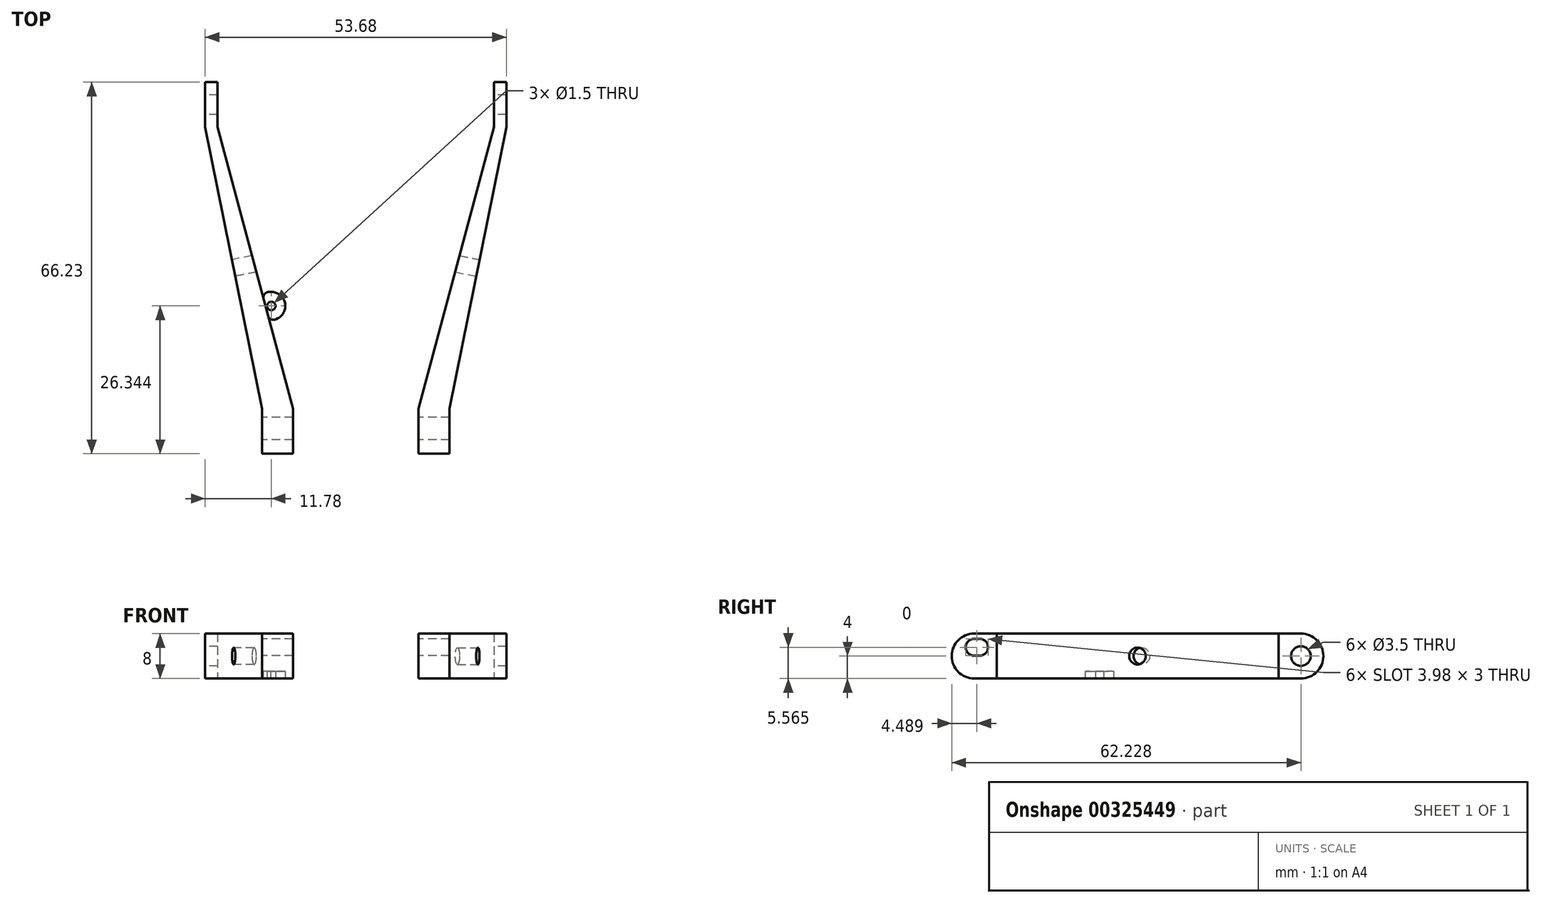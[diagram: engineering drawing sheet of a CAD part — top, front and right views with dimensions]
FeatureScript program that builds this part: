
annotation { "Feature Type Name" : "Feature", "Feature Type Description" : "" }
export const myFeature = defineFeature(function(context is Context, id is Id, definition is map)
    precondition{}
    {
        {
            var Q0;
            Q0=qCreatedBy(makeId("Top.planeOp"),FACE);
            var sketch = newSketch(context, id + "F0", { "sketchPlane" : qUnion([Q0])});
            skLineSegment(sketch, "E0.bottom", {"start": v(2.75, 4) * mm, "end": v(-2.75, 4) * mm});
            skLineSegment(sketch, "E0.top", {"start": v(2.75, -4) * mm, "end": v(-2.75, -4) * mm});
            skLineSegment(sketch, "E0.left", {"start": v(2.75, 4) * mm, "end": v(2.75, -4) * mm});
            skLineSegment(sketch, "E0.right", {"start": v(-2.75, 4) * mm, "end": v(-2.75, -4) * mm});
            skPoint(sketch, "E0.middle", {"position": v(0, 0) * mm});
            skLineSegment(sketch, "E1", {"start": v(2.75, 4) * mm, "end": v(-10.7, 54.23) * mm});
            skLineSegment(sketch, "E2.bottom", {"start": v(-10.7, 54.23) * mm, "end": v(-12.9, 54.23) * mm});
            skLineSegment(sketch, "E2.top", {"start": v(-10.7, 62.23) * mm, "end": v(-12.9, 62.23) * mm});
            skLineSegment(sketch, "E2.left", {"start": v(-10.7, 54.23) * mm, "end": v(-10.7, 62.23) * mm});
            skLineSegment(sketch, "E2.right", {"start": v(-12.9, 54.23) * mm, "end": v(-12.9, 62.23) * mm});
            skLineSegment(sketch, "E3", {"start": v(-12.9, 54.23) * mm, "end": v(-2.75, 4) * mm});
            skCircle(sketch, "E4", {"center": v(-1.13, 22.34) * mm, "radius": 0.75 * mm});
            skArc(sketch, "E5", {"start": v(0, 20.11) * mm, "mid": v(1.28, 23) * mm, "end": v(-1.28, 24.84) * mm});
            skLineSegment(sketch, "E6", {"start": v(-1.28, 24.84) * mm, "end": v(-2.83, 24.84) * mm});
            skLineSegment(sketch, "E7", {"start": v(-2.83, 24.84) * mm, "end": v(-1.38, 19.41) * mm});
            skLineSegment(sketch, "E8", {"start": v(-1.38, 19.41) * mm, "end": v(0, 20.11) * mm});
            skLineSegment(sketch, "E9", {"start": v(13.93, -16.72) * mm, "end": v(13.93, 66.12) * mm});
            skLineSegment(sketch, "E10.MirrorCS", {"start": v(38.57, 54.23) * mm, "end": v(38.57, 62.23) * mm});
            skLineSegment(sketch, "E11.MirrorCS", {"start": v(40.77, 54.23) * mm, "end": v(40.77, 62.23) * mm});
            skLineSegment(sketch, "E12.MirrorCS", {"start": v(40.77, 54.23) * mm, "end": v(30.6, 4) * mm});
            skLineSegment(sketch, "E13.MirrorCS", {"start": v(25.1, 4) * mm, "end": v(38.57, 54.23) * mm});
            skLineSegment(sketch, "E14.MirrorCS", {"start": v(25.1, 4) * mm, "end": v(25.1, -4) * mm});
            skLineSegment(sketch, "E15.MirrorCS", {"start": v(25.1, -4) * mm, "end": v(30.6, -4) * mm});
            skLineSegment(sketch, "E16.MirrorCS", {"start": v(30.6, 4) * mm, "end": v(30.6, -4) * mm});
            skArc(sketch, "E17.MirrorCS", {"start": v(27.86, 20.11) * mm, "mid": v(26.58, 23) * mm, "end": v(29.14, 24.84) * mm});
            skLineSegment(sketch, "E18.MirrorCS", {"start": v(29.14, 24.84) * mm, "end": v(30.7, 24.84) * mm});
            skLineSegment(sketch, "E19.MirrorCS", {"start": v(29.24, 19.41) * mm, "end": v(27.86, 20.11) * mm});
            skCircle(sketch, "E20.MirrorC", {"center": v(28.99, 22.34) * mm, "radius": 0.75 * mm});
            skLineSegment(sketch, "E21.MirrorCS", {"start": v(38.57, 62.23) * mm, "end": v(40.77, 62.23) * mm});
            skSolve(sketch);
        }
        {
            var Q0;
            {var subQ3=sQuery(id+"F0.wireOp",EDGE,"E10.MirrorCS");Q0=makeQuery(id+"F0.imprint","IMPRINT",FACE,{"disambiguationData":[TD([[makeQuery(id+"F0.imprint","IMPRINT",EDGE,{"derivedFrom":subQ3}),-1.0]])]});}
            var Q1;
            {var subQ2=sQuery(id+"F0.wireOp",EDGE,"E0.bottom");Q1=makeQuery(id+"F0.imprint","IMPRINT",FACE,{"disambiguationData":[TD([[makeQuery(id+"F0.imprint","IMPRINT",EDGE,{"derivedFrom":subQ2}),-1.0]])]});}
            var Q2;
            Q2=makeQuery(id+"F0.imprint","IMPRINT",FACE,{"disambiguationData":[TD([[makeQuery(id+"F0.imprint","IMPRINT",EDGE,{"derivedFrom":sQuery(id+"F0.wireOp",EDGE,"E2.bottom")}),-1.0]])]});
            var Q3;
            Q3=makeQuery(id+"F0.imprint","IMPRINT",FACE,{"disambiguationData":[TD([[makeQuery(id+"F0.imprint","IMPRINT",EDGE,{"derivedFrom":sQuery(id+"F0.wireOp",EDGE,"E0.bottom")}),1.0]])]});
            extrude(context, id + "F1", {"entities" : qUnion([Q0, Q1, Q2, Q3]), "depth" : 8 * mm});
        }
        {
            var Q0;
            Q0=makeQuery(id+"F0.imprint","IMPRINT",FACE,{"disambiguationData":[TD([[makeQuery(id+"F0.imprint","IMPRINT",EDGE,{"derivedFrom":sQuery(id+"F0.wireOp",EDGE,"E4")}),-1.0]])]});
            var Q1;
            Q1=makeQuery(id+"F0.imprint","IMPRINT",FACE,{"disambiguationData":[TD([[makeQuery(id+"F0.imprint","IMPRINT",EDGE,{"derivedFrom":sQuery(id+"F0.wireOp",EDGE,"E17.MirrorCS")}),-1.0]])]});
            extrude(context, id + "F2", {"entities" : qUnion([Q0, Q1]), "depth" : 1.3 * mm});
        }
        {
            var Q0;
            Q0=makeQuery(id+"F1.opExtrude","SWEPT_FACE",FACE,{"disambiguationData":[OSD([sQuery(id+"F0.wireOp",EDGE,"E2.right")])]});
            var sketch = newSketch(context, id + "F3", { "sketchPlane" : qUnion([Q0])});
            skCircle(sketch, "E22", {"center": v(-58.23, 4) * mm, "radius": 1.75 * mm});
            skPoint(sketch, "E22.centerSnap0", {"position": v(-58.23, 8) * mm});
            skPoint(sketch, "E22.centerSnap1", {"position": v(-62.23, 4) * mm});
            skArc(sketch, "E23", {"start": v(0, 4.06) * mm, "mid": v(1.5, 5.56) * mm, "end": v(0, 7.06) * mm});
            skArc(sketch, "E24", {"start": v(-0.98, 7.06) * mm, "mid": v(-2.48, 5.56) * mm, "end": v(-0.98, 4.06) * mm});
            skLineSegment(sketch, "E25", {"start": v(-0.98, 4.06) * mm, "end": v(0, 4.06) * mm});
            skLineSegment(sketch, "E26", {"start": v(-0.98, 7.06) * mm, "end": v(0, 7.06) * mm});
            skSolve(sketch);
        }
        {
            var Q0;
            Q0=makeQuery(id+"F3.imprint","IMPRINT",FACE,{"disambiguationData":[TD([[makeQuery(id+"F3.imprint","IMPRINT",EDGE,{"derivedFrom":sQuery(id+"F3.wireOp",EDGE,"E23")}),1.0]])]});
            var Q1;
            Q1=makeQuery(id+"F3.imprint","IMPRINT",FACE,{"disambiguationData":[TD([[makeQuery(id+"F3.imprint","IMPRINT",EDGE,{"derivedFrom":sQuery(id+"F3.wireOp",EDGE,"E22")}),1.0]])]});
            extrude(context, id + "F4", {"entities" : qUnion([Q0, Q1]), "operationType" : NewBodyOperationType.REMOVE, "endBound" : BoundingType.THROUGH_ALL, "oppositeDirection" : true, "depth" : 25 * mm});
        }
        {
            var Q0;
            Q0=makeQuery(id+"F1.opExtrude","SWEPT_FACE",FACE,{"disambiguationData":[OSD([sQuery(id+"F0.wireOp",EDGE,"E3")])]});
            var sketch = newSketch(context, id + "F5", { "sketchPlane" : qUnion([Q0])});
            skCircle(sketch, "E27", {"center": v(-30.09, 4) * mm, "radius": 1.5 * mm});
            skPoint(sketch, "E27.centerSnap0", {"position": v(-30.09, 8) * mm});
            skPoint(sketch, "E27.centerSnap1", {"position": v(-55.71, 4) * mm});
            skSolve(sketch);
        }
        {
            var Q0;
            Q0=makeQuery(id+"F5.imprint","IMPRINT",FACE,{"disambiguationData":[TD([[makeQuery(id+"F5.imprint","IMPRINT",EDGE,{"derivedFrom":sQuery(id+"F5.wireOp",EDGE,"E27")}),1.0]])]});
            extrude(context, id + "F6", {"entities" : qUnion([Q0]), "operationType" : NewBodyOperationType.REMOVE, "oppositeDirection" : true, "depth" : 25 * mm});
        }
        {
            var Q0;
            Q0=makeQuery(id+"F1.opExtrude","SWEPT_FACE",FACE,{"disambiguationData":[OSD([sQuery(id+"F0.wireOp",EDGE,"E12.MirrorCS")])]});
            var sketch = newSketch(context, id + "F7", { "sketchPlane" : qUnion([Q0])});
            skCircle(sketch, "E28", {"center": v(35.61, 4) * mm, "radius": 1.5 * mm});
            skPoint(sketch, "E28.centerSnap0", {"position": v(35.61, 8) * mm});
            skPoint(sketch, "E28.centerSnap1", {"position": v(61.23, 4) * mm});
            skSolve(sketch);
        }
        {
            var Q0;
            Q0=makeQuery(id+"F7.imprint","IMPRINT",FACE,{"disambiguationData":[TD([[makeQuery(id+"F7.imprint","IMPRINT",EDGE,{"derivedFrom":sQuery(id+"F7.wireOp",EDGE,"E28")}),1.0]])]});
            extrude(context, id + "F8", {"entities" : qUnion([Q0]), "operationType" : NewBodyOperationType.REMOVE, "oppositeDirection" : true, "depth" : 25 * mm});
        }
        {
            var Q0;
            Q0=makeQuery(id+"F1.opExtrude","CAP_EDGE",EDGE,{"disambiguationData":[OSD([sQuery(id+"F0.wireOp",EDGE,"E2.top")])],"isStart":false});
            var Q1;
            Q1=makeQuery(id+"F1.opExtrude","CAP_EDGE",EDGE,{"disambiguationData":[OSD([sQuery(id+"F0.wireOp",EDGE,"E0.top")])],"isStart":false});
            var Q2;
            Q2=makeQuery(id+"F1.opExtrude","CAP_EDGE",EDGE,{"disambiguationData":[OSD([sQuery(id+"F0.wireOp",EDGE,"E15.MirrorCS")])],"isStart":false});
            var Q3;
            Q3=makeQuery(id+"F1.opExtrude","CAP_EDGE",EDGE,{"disambiguationData":[OSD([sQuery(id+"F0.wireOp",EDGE,"E21.MirrorCS")])],"isStart":false});
            var Q4;
            Q4=makeQuery(id+"F1.opExtrude","CAP_EDGE",EDGE,{"disambiguationData":[OSD([sQuery(id+"F0.wireOp",EDGE,"E2.top")])],"isStart":true});
            var Q5;
            Q5=makeQuery(id+"F1.opExtrude","CAP_EDGE",EDGE,{"disambiguationData":[OSD([sQuery(id+"F0.wireOp",EDGE,"E21.MirrorCS")])],"isStart":true});
            var Q6;
            Q6=makeQuery(id+"F1.opExtrude","CAP_EDGE",EDGE,{"disambiguationData":[OSD([sQuery(id+"F0.wireOp",EDGE,"E15.MirrorCS")])],"isStart":true});
            var Q7;
            Q7=makeQuery(id+"F1.opExtrude","CAP_EDGE",EDGE,{"disambiguationData":[OSD([sQuery(id+"F0.wireOp",EDGE,"E0.top")])],"isStart":true});
            fillet(context, id + "F9", {"entities" : qUnion([Q0, Q1, Q2, Q3, Q4, Q5, Q6, Q7]), "radius" : 4 * mm, "tangentPropagation" : true, "allowEdgeOverflow" : false});
        }
        {
            var Q0;
            Q0=makeQuery(id+"F2.opExtrude","CAP_EDGE",EDGE,{"disambiguationData":[OSD([sQuery(id+"F0.wireOp",EDGE,"E13.MirrorCS")])],"isStart":false});
            var Q1;
            Q1=makeQuery(id+"F2.opExtrude","SWEPT_EDGE",EDGE,{"disambiguationData":[OSD([sQuery(id+"F0.wireOp",EDGE,"E13.MirrorCS"),sQuery(id+"F0.wireOp",EDGE,"E18.MirrorCS")])]});
            var Q2;
            Q2=makeQuery(id+"F2.opExtrude","SWEPT_EDGE",EDGE,{"disambiguationData":[OSD([sQuery(id+"F0.wireOp",EDGE,"E13.MirrorCS"),sQuery(id+"F0.wireOp",EDGE,"E19.MirrorCS")])]});
            var Q3;
            Q3=makeQuery(id+"F2.opExtrude","SWEPT_EDGE",EDGE,{"disambiguationData":[OSD([sQuery(id+"F0.wireOp",EDGE,"E1"),sQuery(id+"F0.wireOp",EDGE,"E7"),sQuery(id+"F0.wireOp",EDGE,"E8")])]});
            var Q4;
            Q4=makeQuery(id+"F2.opExtrude","CAP_EDGE",EDGE,{"disambiguationData":[OSD([sQuery(id+"F0.wireOp",EDGE,"E7")])],"isStart":false});
            var Q5;
            Q5=makeQuery(id+"F2.opExtrude","SWEPT_EDGE",EDGE,{"disambiguationData":[OSD([sQuery(id+"F0.wireOp",EDGE,"E1"),sQuery(id+"F0.wireOp",EDGE,"E6"),sQuery(id+"F0.wireOp",EDGE,"E7")])]});
            fillet(context, id + "F10", {"entities" : qUnion([Q0, Q1, Q2, Q3, Q4, Q5]), "radius" : 1 * mm, "tangentPropagation" : true, "allowEdgeOverflow" : false});
        }
    });
